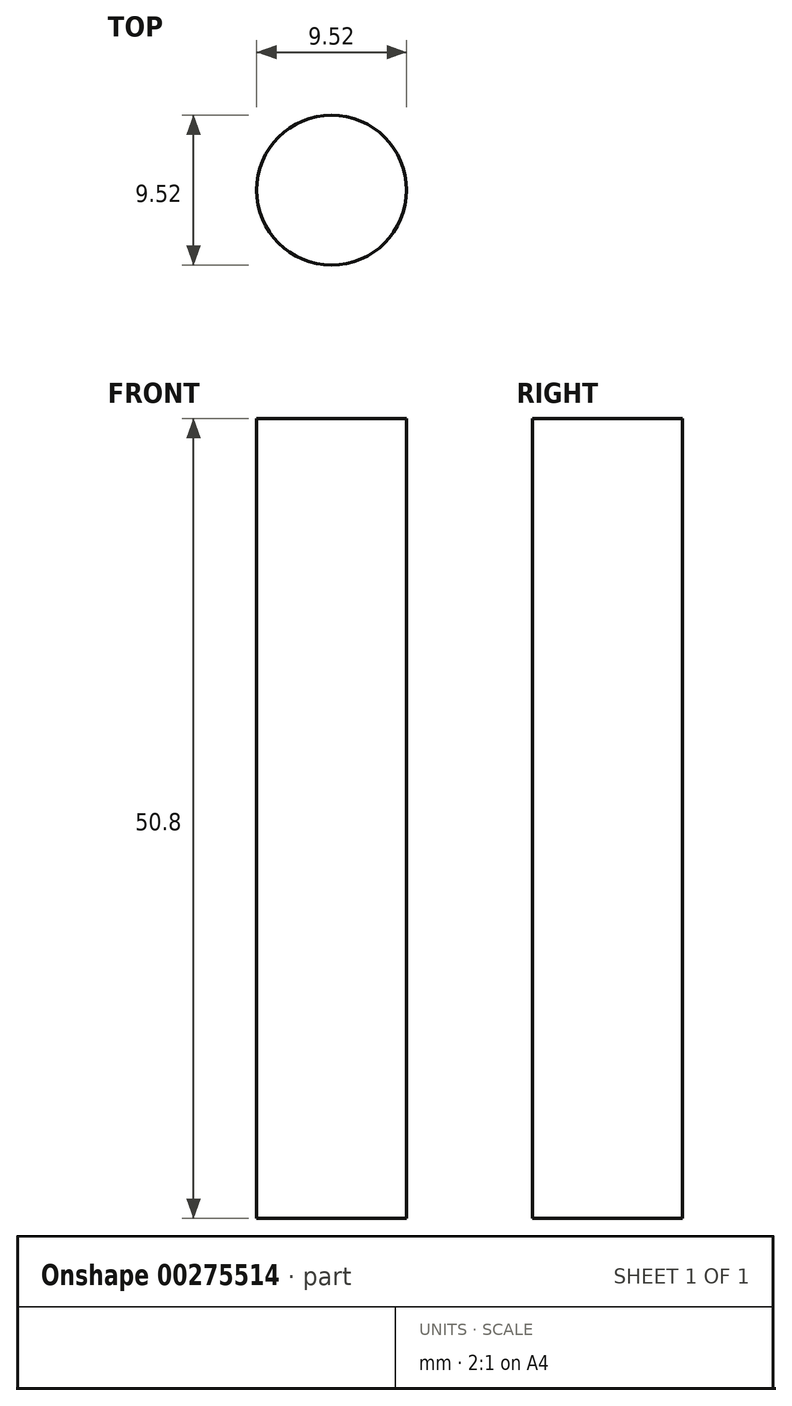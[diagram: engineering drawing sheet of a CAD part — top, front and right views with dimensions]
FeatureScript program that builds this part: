
annotation { "Feature Type Name" : "Feature", "Feature Type Description" : "" }
export const myFeature = defineFeature(function(context is Context, id is Id, definition is map)
    precondition{}
    {
        {
            var Q0;
            Q0=qCreatedBy(makeId("Top.planeOp"),FACE);
            var sketch = newSketch(context, id + "F0", { "sketchPlane" : qUnion([Q0])});
            skCircle(sketch, "E0", {"center": v(0, 0) * mm, "radius": 4.76 * mm});
            skSolve(sketch);
        }
        {
            var Q0;
            Q0 = qSketchRegion(id + "F0", true);
            extrude(context, id + "F1", {"entities" : qUnion([Q0]), "depth" : 50.8 * mm});
        }
    });
